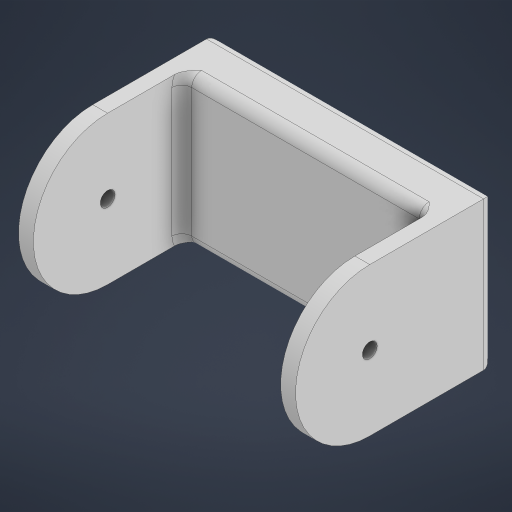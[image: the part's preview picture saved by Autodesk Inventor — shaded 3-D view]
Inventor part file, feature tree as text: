
AUTODESK INVENTOR PART (.ipt)
format: ipt  version: 2023 (Build 270158000, 158)  size: 238,080 bytes
history: native  units: mm
features: extrude x6, sketch x6, fillet x3
ambient origin geometry x8: Origin, YZ Plane, XZ Plane, XY Plane, X Axis, Y Axis, Z Axis, Center Point
bodies: Solid1 (feature_tree)
feature tree (15):
  extrude  "Extrusion1"  Depth=30.0mm
  extrude  "Extrusion2"  Depth=10.0mm
  fillet  "Fillet1"  Radius=15.0mm
  extrude  "Extrusion3"  Depth=30.0mm TaperAngle=0.0deg
  extrude  "Extrusion4"  Depth=10.0mm TaperAngle=0.0deg
  fillet  "Fillet3"  Radius=15.0mm
  extrude  "Extrusion5"  Depth=2.0mm
  fillet  "Fillet4"  [1 undecoded]
  extrude  "Extrusion6"  Depth=5.0mm
  sketch  "Sketch1"  dims[d0=50.0mm d1=30.0mm]
  sketch  "Sketch2"  dims[d2=10.0mm d3=0.0mm d4=3.0mm]
  sketch  "Sketch3"  dims[d5=30.0mm d6=10.0mm d7=0.0mm d8=0.0mm d9=15.0mm]
  sketch  "Sketch4"  dims[d10=3.0mm d11=30.0mm d12=0.0mm]
  sketch  "Sketch5"  dims[d14=3.0mm d15=30.0mm d16=10.0mm d17=0.0mm d18=0.0mm d19=15.0mm]
  sketch  "Sketch6"  dims[d20=30.0mm d21=0.0mm d22=2.0mm d23=180.0deg d24=16.0mm d25=5.0mm d26=0.0mm]
note: 1 required parameter value undecoded (feature->parameter linkage not recoverable at this tier; creation-order binding heuristic only, values carry confidence <= 0.55)
